# Revit family: Flush_Valve-Sensor-Hardwired-Zurn-Exposed-Urinal-ZEMS6003AV-IS
name_source: partatom
category: Plumbing Fixtures
units: mm (PartAtom-declared; Revit-internal decimal feet)

## family parameters
Cut with Voids When Loaded = No
Host = Face
Maintain Annotation Orientation = No
OmniClass Number = 23.45.05.14.99
OmniClass Title = Other Sanitary Washing Plumbing Fixtures
Part Type = Normal
Room Calculation Point = No
Round Connector Dimension = Use Radius
Shared = No

## types (12) — shared parameters
Activation Method = Sensor Operated
Assembly Code = D2010.60
CW Connection = Yes
CWFU = 1
Centerline of Stop Valve to Centerline of Flush Valve = 4.75 "
Default Elevation = 48 "
Description = Exposed Hardwired Automatic Sensor Flush Valve Urinal with Integral Sensor
HW Connection = No
Inlet Connection Size (inch) = 1 "
Main Material = Chrome-Plated Brass - Zurn - Polished
Manufacturer = Zurn Water, LLC
Manufacturer Brand = Zurn
Max Working Water Temperature = 104 °F
Model = ZEMS6003AV-IS
Modified Date = 01/08/2026
Operating Water Pressure (PSI) = 25 – 80 PSI (172 – 552 kPa)
Product Documentation Link = https://files.zurn.com
Product Installation Sheet URL = https://files.zurn.com
Product Page URL = https://www.zurn.com
Product data URL = https://www.bimobject.com
Repair Parts URL = https://files.zurn.com
URL = https://www.zurn.com
Vent Connection = No
Waste Connection = No
zero-valued in all types: HWFU, WFU

## per-type parameters (varying)
| type | Flush Rate (GPF) | Type Comments |
| ZEMS6003AV-ULF-IS (0.125 GPF, 11-1/2") | 0.125 GPF | ZEMS6003AV-ULF-IS (0.125 GPF, 11-1/2" R-I) |
| ZEMS6003AV-EWS-IS (0.5 GPF, 11-1/2") | 0.5 GPF | ZEMS6003AV-EWS-IS (0.5 GPF, 11-1/2" R-I) |
| ZEMS6003AV-WS1-IS (1.0 GPF, 11-1/2") | 1.0 GPF | ZEMS6003AV-WS1-IS (1.0 GPF, 11-1/2" R-I) |
| ZEMS6003AV-IS (1.5 GPF, 11-1/2") | 1.5 GPF | ZEMS6003AV-IS (1.5 GPF, 11-1/2" R-I) |
| ZEMS6003AV-1-ULF-IS (0.125 GPF, 16") | 0.125 GPF | ZEMS6003AV-1-ULF-IS (0.125 GPF, 16" R-I) |
| ZEMS6003AV-1-EWS-IS (0.5 GPF, 16") | 0.5 GPF | ZEMS6003AV-1-EWS-IS (0.5 GPF, 16" R-I) |
| ZEMS6003AV-1-WS1-IS (1.0 GPF, 16") | 1.0 GPF | ZEMS6003AV-1-WS1-IS (1.0 GPF, 16" R-I) |
| ZEMS6003AV-1-IS (1.5 GPF, 16") | 1.5 GPF | ZEMS6003AV-1-IS (1.5 GPF, 16" R-I) |
| ZEMS6003AV-2-ULF-IS (0.125 GPF, 24") | 0.125 GPF | ZEMS6003AV-2-ULF-IS (0.125 GPF, 24" R-I) |
| ZEMS6003AV-2-EWS-IS (0.5 GPF, 24") | 0.5 GPF | ZEMS6003AV-2-EWS-IS (0.5 GPF, 24" R-I) |
| ZEMS6003AV-2-WS1-IS (1.0 GPF, 24") | 1.0 GPF | ZEMS6003AV-2-WS1-IS (1.0 GPF, 24" R-I) |
| ZEMS6003AV-2-IS (1.5 GPF, 24") | 1.5 GPF | ZEMS6003AV-2-IS (1.5 GPF, 24" R-I) |

## geometry (parser evidence)
native form markers: Blend x8, Sweep x16
no freeform markers — native parametric forms only
